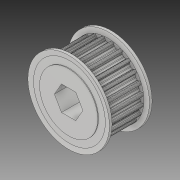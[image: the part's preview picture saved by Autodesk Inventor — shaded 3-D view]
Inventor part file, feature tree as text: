
AUTODESK INVENTOR PART (.ipt)
format: ipt  version: 2019 (Build 230136000, 136)  size: 644,608 bytes
history: native  units: in
note: dims shown in document units (in); Inventor stores cm internally (conversion verified against a paired STEP export)
features: mirror x1
ambient origin geometry x8: Origin, YZ Plane, XZ Plane, XY Plane, X Axis, Y Axis, Z Axis, Center Point
bodies: Solid1 (feature_tree)
feature tree (1):
  mirror  "Mirror1"
